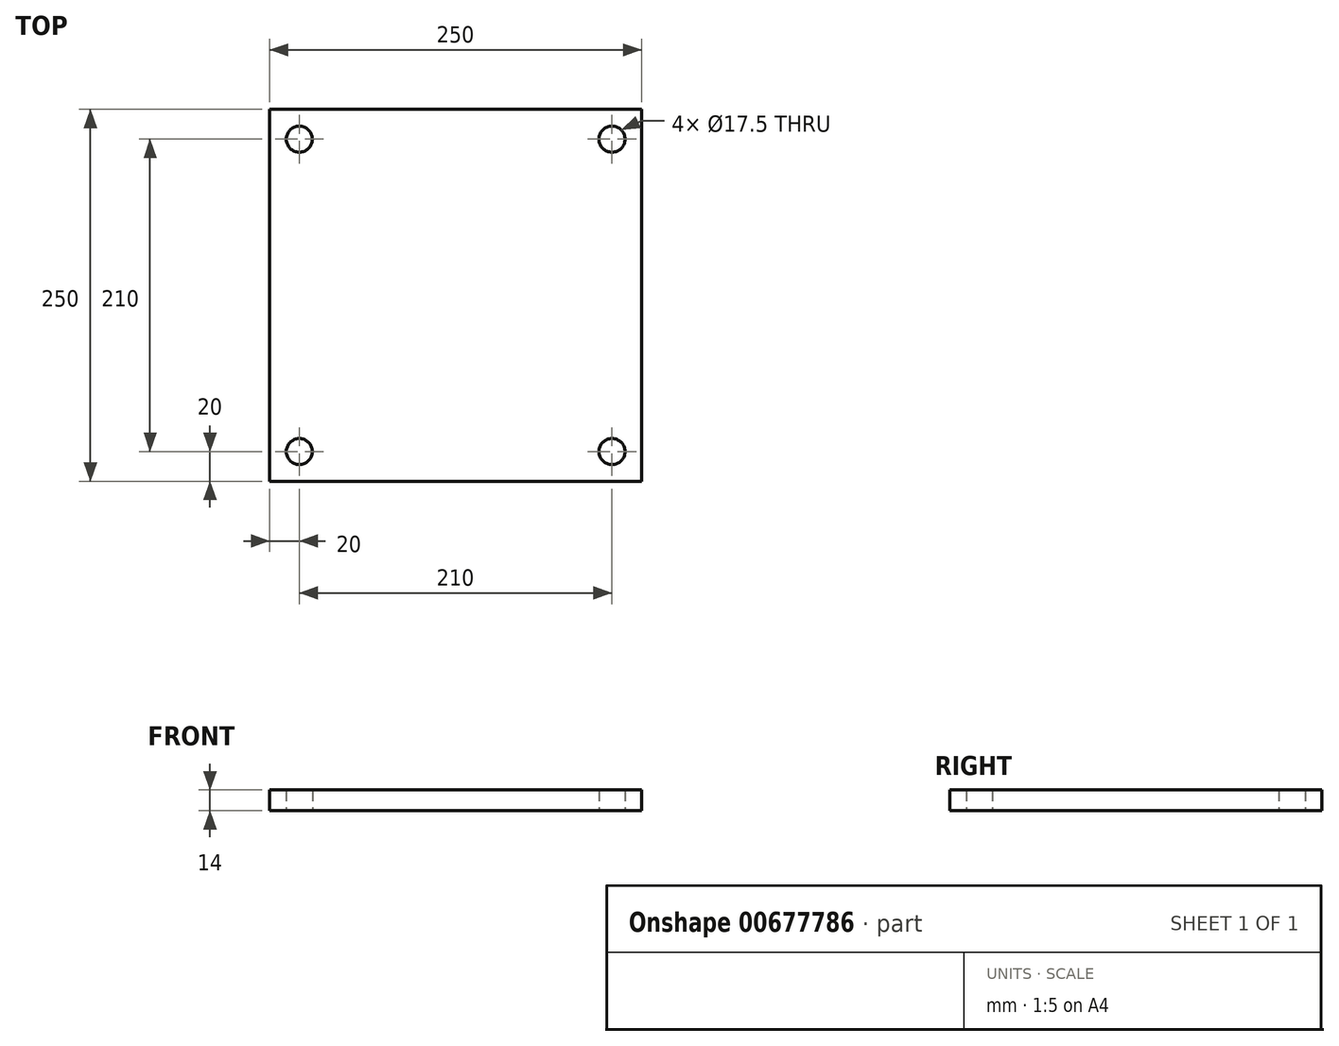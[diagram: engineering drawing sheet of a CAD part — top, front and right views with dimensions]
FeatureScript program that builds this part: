
annotation { "Feature Type Name" : "Feature", "Feature Type Description" : "" }
export const myFeature = defineFeature(function(context is Context, id is Id, definition is map)
    precondition{}
    {
        {
            var Q0;
            Q0=qCreatedBy(makeId("Top.planeOp"),FACE);
            var sketch = newSketch(context, id + "F0", { "sketchPlane" : qUnion([Q0])});
            skLineSegment(sketch, "E0.bottom", {"start": v(125, -125) * mm, "end": v(-125, -125) * mm});
            skLineSegment(sketch, "E0.top", {"start": v(125, 125) * mm, "end": v(-125, 125) * mm});
            skLineSegment(sketch, "E0.left", {"start": v(125, -125) * mm, "end": v(125, 125) * mm});
            skLineSegment(sketch, "E0.right", {"start": v(-125, -125) * mm, "end": v(-125, 125) * mm});
            skPoint(sketch, "E0.middle", {"position": v(0, 0) * mm});
            skPoint(sketch, "E1", {"position": v(-105, -105) * mm});
            skPoint(sketch, "E2.MirrorP", {"position": v(105, -105) * mm});
            skPoint(sketch, "E3.MirrorP", {"position": v(-105, 105) * mm});
            skPoint(sketch, "E4.MirrorP", {"position": v(105, 105) * mm});
            skSolve(sketch);
        }
        {
            var Q0;
            Q0=makeQuery(id+"F0.imprint","IMPRINT",FACE,{"disambiguationData":[TD([[makeQuery(id+"F0.imprint","IMPRINT",EDGE,{"derivedFrom":sQuery(id+"F0.wireOp",EDGE,"E0.bottom")}),-1.0]])]});
            extrude(context, id + "F1", {"entities" : qUnion([Q0]), "depth" : 14 * mm, "offsetDistance" : 25 * mm});
        }
        {
            var Q0;
            Q0=sQuery(id+"F0.wireOp",VERTEX,"E1");
            var Q1;
            Q1=sQuery(id+"F0.wireOp",VERTEX,"E2.MirrorP");
            var Q2;
            Q2=sQuery(id+"F0.wireOp",VERTEX,"E3.MirrorP");
            var Q3;
            Q3=sQuery(id+"F0.wireOp",VERTEX,"E4.MirrorP");
            var Q4;
            Q4=makeQuery(id+"F1.opExtrude","SWEPT_BODY",BODY,{"disambiguationData":[OSD([sQuery(id+"F0.wireOp",EDGE,"E0.bottom"),sQuery(id+"F0.wireOp",EDGE,"E0.top"),sQuery(id+"F0.wireOp",EDGE,"E0.left"),sQuery(id+"F0.wireOp",EDGE,"E0.right")])]});
            hole(context, id + "F2", {"style" : HoleStyle.SIMPLE, "endStyle" : HoleEndStyle.THROUGH, "oppositeDirection" : true, "standardTappedOrClearance" : lookupTablePath({ "standard" : "ISO", "fit" : "Normal", "size" : "M16", "type" : "Clearance" }), "standardBlindInLast" : lookupTablePath({ "fit" : "Standard", "standard" : "ISO", "size" : "M16", "type" : "Clearance" }), "holeDiameter" : 17.5 * mm, "majorDiameter" : 5 * mm, "isTappedThrough" : true, "tappedDepth" : 12 * mm, "tapClearance" : 3, "locations" : qUnion([Q0, Q1, Q2, Q3]), "scope" : qUnion([Q4])});
        }
    });
